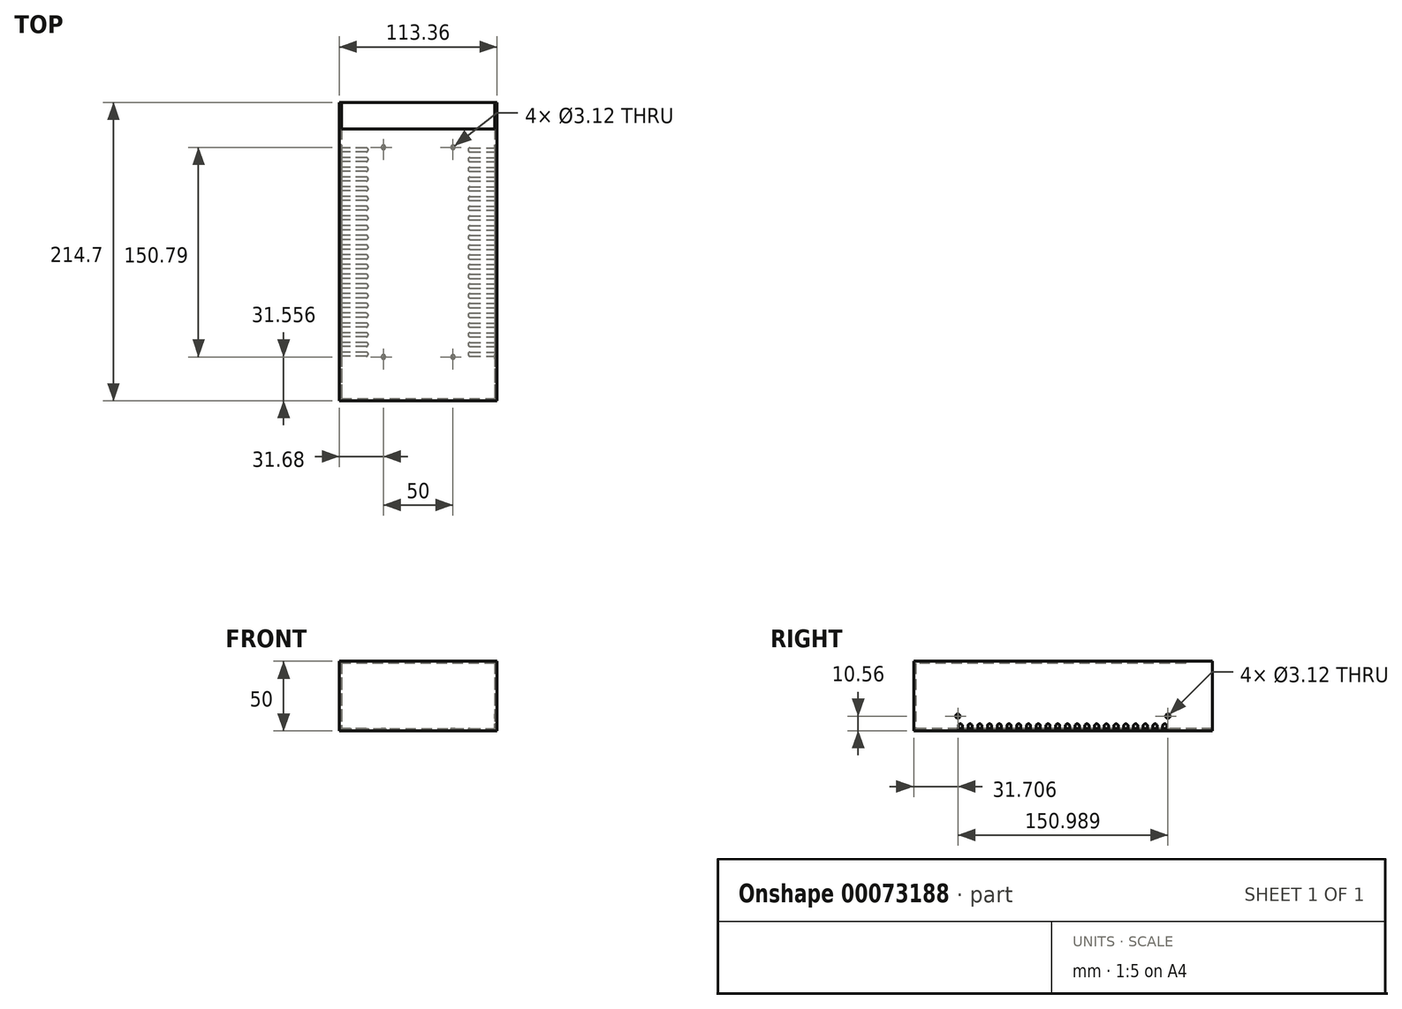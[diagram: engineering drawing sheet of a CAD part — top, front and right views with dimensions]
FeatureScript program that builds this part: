
annotation { "Feature Type Name" : "Feature", "Feature Type Description" : "" }
export const myFeature = defineFeature(function(context is Context, id is Id, definition is map)
    precondition{}
    {
        {
            var Q0;
            Q0=qCreatedBy(makeId("Top.planeOp"),FACE);
            var sketch = newSketch(context, id + "F0", { "sketchPlane" : qUnion([Q0])});
            skLineSegment(sketch, "E0.bottom", {"start": v(-56.68, 107.35) * mm, "end": v(56.67, 107.35) * mm});
            skLineSegment(sketch, "E0.top", {"start": v(-56.67, -107.35) * mm, "end": v(56.68, -107.35) * mm});
            skLineSegment(sketch, "E0.left", {"start": v(-56.68, 107.35) * mm, "end": v(-56.67, -107.35) * mm});
            skLineSegment(sketch, "E0.right", {"start": v(56.67, 107.35) * mm, "end": v(56.68, -107.35) * mm});
            skSolve(sketch);
        }
        {
            var Q0;
            Q0 = qSketchRegion(id + "F0", true);
            extrude(context, id + "F1", {"entities" : qUnion([Q0]), "depth" : 50 * mm});
        }
        {
            var Q0;
            Q0=makeQuery(id+"F1.opExtrude","CAP_FACE",FACE,{"disambiguationData":[OSD([sQuery(id+"F0.wireOp",EDGE,"E0.bottom"),sQuery(id+"F0.wireOp",EDGE,"E0.top"),sQuery(id+"F0.wireOp",EDGE,"E0.left"),sQuery(id+"F0.wireOp",EDGE,"E0.right")])],"isStart":true});
            var sketch = newSketch(context, id + "F2", { "sketchPlane" : qUnion([Q0])});
            skCircle(sketch, "E1", {"center": v(25, -75) * mm, "radius": 1.56 * mm});
            skCircle(sketch, "E2", {"center": v(-25, -75) * mm, "radius": 1.56 * mm});
            skCircle(sketch, "E3", {"center": v(25, 75.8) * mm, "radius": 1.56 * mm});
            skCircle(sketch, "E4", {"center": v(-25, 75.8) * mm, "radius": 1.56 * mm});
            skSolve(sketch);
        }
        {
            var Q0;
            Q0=makeQuery(id+"F1.opExtrude","SWEPT_FACE",FACE,{"disambiguationData":[OSD([sQuery(id+"F0.wireOp",EDGE,"E0.bottom")])]});
            shell(context, id + "F3", {"entities" : qUnion([Q0]), "thickness" : 1.5 * mm});
        }
        {
            var Q0;
            Q0 = qSketchRegion(id + "F2", true);
            extrude(context, id + "F4", {"entities" : qUnion([Q0]), "operationType" : NewBodyOperationType.REMOVE, "endBound" : BoundingType.UP_TO_NEXT, "oppositeDirection" : true, "depth" : 25 * mm});
        }
        {
            var Q0;
            Q0=makeQuery(id+"F1.opExtrude","CAP_FACE",FACE,{"disambiguationData":[OSD([sQuery(id+"F0.wireOp",EDGE,"E0.bottom"),sQuery(id+"F0.wireOp",EDGE,"E0.top"),sQuery(id+"F0.wireOp",EDGE,"E0.left"),sQuery(id+"F0.wireOp",EDGE,"E0.right")])],"isStart":true});
            var sketch = newSketch(context, id + "F5", { "sketchPlane" : qUnion([Q0])});
            skLineSegment(sketch, "E5.bottom", {"start": v(-37.4, 72.35) * mm, "end": v(-56.67, 72.35) * mm});
            skLineSegment(sketch, "E5.top", {"start": v(-37.4, 75.35) * mm, "end": v(-56.67, 75.35) * mm});
            skLineSegment(sketch, "E5.left", {"start": v(-37.4, 72.35) * mm, "end": v(-37.4, 75.35) * mm});
            skLineSegment(sketch, "E5.right", {"start": v(-56.67, 72.35) * mm, "end": v(-56.67, 75.35) * mm});
            skCircle(sketch, "E6", {"center": v(-37.4, 73.85) * mm, "radius": 1.5 * mm});
            skLineSegment(sketch, "E7.MirrorCS", {"start": v(37.4, 72.35) * mm, "end": v(56.67, 72.35) * mm});
            skLineSegment(sketch, "E8.MirrorCS", {"start": v(37.4, 75.35) * mm, "end": v(56.67, 75.35) * mm});
            skLineSegment(sketch, "E9.MirrorCS", {"start": v(56.67, 72.35) * mm, "end": v(56.67, 75.35) * mm});
            skCircle(sketch, "E10.MirrorC", {"center": v(37.4, 73.85) * mm, "radius": 1.5 * mm});
            skLineSegment(sketch, "E11.0.1.0", {"start": v(-37.4, 65.35) * mm, "end": v(-56.67, 65.35) * mm});
            skCircle(sketch, "E11.0.1.1", {"center": v(-37.4, 66.85) * mm, "radius": 1.5 * mm});
            skLineSegment(sketch, "E11.0.1.2", {"start": v(-37.4, 68.35) * mm, "end": v(-56.67, 68.35) * mm});
            skLineSegment(sketch, "E11.0.1.3", {"start": v(-56.67, 65.35) * mm, "end": v(-56.67, 68.35) * mm});
            skCircle(sketch, "E11.0.1.4", {"center": v(37.4, 66.85) * mm, "radius": 1.5 * mm});
            skLineSegment(sketch, "E11.0.1.5", {"start": v(37.4, 65.35) * mm, "end": v(56.67, 65.35) * mm});
            skLineSegment(sketch, "E11.0.1.6", {"start": v(37.4, 68.35) * mm, "end": v(56.67, 68.35) * mm});
            skLineSegment(sketch, "E11.0.1.7", {"start": v(56.67, 65.35) * mm, "end": v(56.67, 68.35) * mm});
            skLineSegment(sketch, "E11.0.2.0", {"start": v(-37.4, 58.35) * mm, "end": v(-56.67, 58.35) * mm});
            skCircle(sketch, "E11.0.2.1", {"center": v(-37.4, 59.85) * mm, "radius": 1.5 * mm});
            skLineSegment(sketch, "E11.0.2.2", {"start": v(-37.4, 61.35) * mm, "end": v(-56.67, 61.35) * mm});
            skLineSegment(sketch, "E11.0.2.3", {"start": v(-56.67, 58.35) * mm, "end": v(-56.67, 61.35) * mm});
            skCircle(sketch, "E11.0.2.4", {"center": v(37.4, 59.85) * mm, "radius": 1.5 * mm});
            skLineSegment(sketch, "E11.0.2.5", {"start": v(37.4, 58.35) * mm, "end": v(56.67, 58.35) * mm});
            skLineSegment(sketch, "E11.0.2.6", {"start": v(37.4, 61.35) * mm, "end": v(56.67, 61.35) * mm});
            skLineSegment(sketch, "E11.0.2.7", {"start": v(56.67, 58.35) * mm, "end": v(56.67, 61.35) * mm});
            skLineSegment(sketch, "E11.0.3.0", {"start": v(-37.4, 51.35) * mm, "end": v(-56.67, 51.35) * mm});
            skCircle(sketch, "E11.0.3.1", {"center": v(-37.4, 52.85) * mm, "radius": 1.5 * mm});
            skLineSegment(sketch, "E11.0.3.2", {"start": v(-37.4, 54.35) * mm, "end": v(-56.67, 54.35) * mm});
            skLineSegment(sketch, "E11.0.3.3", {"start": v(-56.67, 51.35) * mm, "end": v(-56.67, 54.35) * mm});
            skCircle(sketch, "E11.0.3.4", {"center": v(37.4, 52.85) * mm, "radius": 1.5 * mm});
            skLineSegment(sketch, "E11.0.3.5", {"start": v(37.4, 51.35) * mm, "end": v(56.67, 51.35) * mm});
            skLineSegment(sketch, "E11.0.3.6", {"start": v(37.4, 54.35) * mm, "end": v(56.67, 54.35) * mm});
            skLineSegment(sketch, "E11.0.3.7", {"start": v(56.67, 51.35) * mm, "end": v(56.67, 54.35) * mm});
            skLineSegment(sketch, "E11.0.4.0", {"start": v(-37.4, 44.35) * mm, "end": v(-56.67, 44.35) * mm});
            skCircle(sketch, "E11.0.4.1", {"center": v(-37.4, 45.85) * mm, "radius": 1.5 * mm});
            skLineSegment(sketch, "E11.0.4.2", {"start": v(-37.4, 47.35) * mm, "end": v(-56.67, 47.35) * mm});
            skLineSegment(sketch, "E11.0.4.3", {"start": v(-56.67, 44.35) * mm, "end": v(-56.67, 47.35) * mm});
            skCircle(sketch, "E11.0.4.4", {"center": v(37.4, 45.85) * mm, "radius": 1.5 * mm});
            skLineSegment(sketch, "E11.0.4.5", {"start": v(37.4, 44.35) * mm, "end": v(56.67, 44.35) * mm});
            skLineSegment(sketch, "E11.0.4.6", {"start": v(37.4, 47.35) * mm, "end": v(56.67, 47.35) * mm});
            skLineSegment(sketch, "E11.0.4.7", {"start": v(56.67, 44.35) * mm, "end": v(56.67, 47.35) * mm});
            skLineSegment(sketch, "E11.0.5.0", {"start": v(-37.4, 37.35) * mm, "end": v(-56.67, 37.35) * mm});
            skCircle(sketch, "E11.0.5.1", {"center": v(-37.4, 38.85) * mm, "radius": 1.5 * mm});
            skLineSegment(sketch, "E11.0.5.2", {"start": v(-37.4, 40.35) * mm, "end": v(-56.67, 40.35) * mm});
            skLineSegment(sketch, "E11.0.5.3", {"start": v(-56.67, 37.35) * mm, "end": v(-56.67, 40.35) * mm});
            skCircle(sketch, "E11.0.5.4", {"center": v(37.4, 38.85) * mm, "radius": 1.5 * mm});
            skLineSegment(sketch, "E11.0.5.5", {"start": v(37.4, 37.35) * mm, "end": v(56.67, 37.35) * mm});
            skLineSegment(sketch, "E11.0.5.6", {"start": v(37.4, 40.35) * mm, "end": v(56.67, 40.35) * mm});
            skLineSegment(sketch, "E11.0.5.7", {"start": v(56.67, 37.35) * mm, "end": v(56.67, 40.35) * mm});
            skLineSegment(sketch, "E11.0.6.0", {"start": v(-37.4, 30.35) * mm, "end": v(-56.67, 30.35) * mm});
            skCircle(sketch, "E11.0.6.1", {"center": v(-37.4, 31.85) * mm, "radius": 1.5 * mm});
            skLineSegment(sketch, "E11.0.6.2", {"start": v(-37.4, 33.35) * mm, "end": v(-56.67, 33.35) * mm});
            skLineSegment(sketch, "E11.0.6.3", {"start": v(-56.67, 30.35) * mm, "end": v(-56.67, 33.35) * mm});
            skCircle(sketch, "E11.0.6.4", {"center": v(37.4, 31.85) * mm, "radius": 1.5 * mm});
            skLineSegment(sketch, "E11.0.6.5", {"start": v(37.4, 30.35) * mm, "end": v(56.67, 30.35) * mm});
            skLineSegment(sketch, "E11.0.6.6", {"start": v(37.4, 33.35) * mm, "end": v(56.67, 33.35) * mm});
            skLineSegment(sketch, "E11.0.6.7", {"start": v(56.67, 30.35) * mm, "end": v(56.67, 33.35) * mm});
            skLineSegment(sketch, "E11.0.7.0", {"start": v(-37.4, 23.35) * mm, "end": v(-56.67, 23.35) * mm});
            skCircle(sketch, "E11.0.7.1", {"center": v(-37.4, 24.85) * mm, "radius": 1.5 * mm});
            skLineSegment(sketch, "E11.0.7.2", {"start": v(-37.4, 26.35) * mm, "end": v(-56.67, 26.35) * mm});
            skLineSegment(sketch, "E11.0.7.3", {"start": v(-56.67, 23.35) * mm, "end": v(-56.67, 26.35) * mm});
            skCircle(sketch, "E11.0.7.4", {"center": v(37.4, 24.85) * mm, "radius": 1.5 * mm});
            skLineSegment(sketch, "E11.0.7.5", {"start": v(37.4, 23.35) * mm, "end": v(56.67, 23.35) * mm});
            skLineSegment(sketch, "E11.0.7.6", {"start": v(37.4, 26.35) * mm, "end": v(56.67, 26.35) * mm});
            skLineSegment(sketch, "E11.0.7.7", {"start": v(56.67, 23.35) * mm, "end": v(56.67, 26.35) * mm});
            skLineSegment(sketch, "E11.0.8.0", {"start": v(-37.4, 16.35) * mm, "end": v(-56.67, 16.35) * mm});
            skCircle(sketch, "E11.0.8.1", {"center": v(-37.4, 17.85) * mm, "radius": 1.5 * mm});
            skLineSegment(sketch, "E11.0.8.2", {"start": v(-37.4, 19.35) * mm, "end": v(-56.67, 19.35) * mm});
            skLineSegment(sketch, "E11.0.8.3", {"start": v(-56.67, 16.35) * mm, "end": v(-56.67, 19.35) * mm});
            skCircle(sketch, "E11.0.8.4", {"center": v(37.4, 17.85) * mm, "radius": 1.5 * mm});
            skLineSegment(sketch, "E11.0.8.5", {"start": v(37.4, 16.35) * mm, "end": v(56.67, 16.35) * mm});
            skLineSegment(sketch, "E11.0.8.6", {"start": v(37.4, 19.35) * mm, "end": v(56.67, 19.35) * mm});
            skLineSegment(sketch, "E11.0.8.7", {"start": v(56.67, 16.35) * mm, "end": v(56.67, 19.35) * mm});
            skLineSegment(sketch, "E11.0.9.0", {"start": v(-37.4, 9.35) * mm, "end": v(-56.67, 9.35) * mm});
            skCircle(sketch, "E11.0.9.1", {"center": v(-37.4, 10.85) * mm, "radius": 1.5 * mm});
            skLineSegment(sketch, "E11.0.9.2", {"start": v(-37.4, 12.35) * mm, "end": v(-56.67, 12.35) * mm});
            skLineSegment(sketch, "E11.0.9.3", {"start": v(-56.67, 9.35) * mm, "end": v(-56.67, 12.35) * mm});
            skCircle(sketch, "E11.0.9.4", {"center": v(37.4, 10.85) * mm, "radius": 1.5 * mm});
            skLineSegment(sketch, "E11.0.9.5", {"start": v(37.4, 9.35) * mm, "end": v(56.67, 9.35) * mm});
            skLineSegment(sketch, "E11.0.9.6", {"start": v(37.4, 12.35) * mm, "end": v(56.67, 12.35) * mm});
            skLineSegment(sketch, "E11.0.9.7", {"start": v(56.67, 9.35) * mm, "end": v(56.67, 12.35) * mm});
            skLineSegment(sketch, "E11.0.10.0", {"start": v(-37.4, 2.35) * mm, "end": v(-56.67, 2.35) * mm});
            skCircle(sketch, "E11.0.10.1", {"center": v(-37.4, 3.85) * mm, "radius": 1.5 * mm});
            skLineSegment(sketch, "E11.0.10.2", {"start": v(-37.4, 5.35) * mm, "end": v(-56.67, 5.35) * mm});
            skLineSegment(sketch, "E11.0.10.3", {"start": v(-56.67, 2.35) * mm, "end": v(-56.67, 5.35) * mm});
            skCircle(sketch, "E11.0.10.4", {"center": v(37.4, 3.85) * mm, "radius": 1.5 * mm});
            skLineSegment(sketch, "E11.0.10.5", {"start": v(37.4, 2.35) * mm, "end": v(56.67, 2.35) * mm});
            skLineSegment(sketch, "E11.0.10.6", {"start": v(37.4, 5.35) * mm, "end": v(56.67, 5.35) * mm});
            skLineSegment(sketch, "E11.0.10.7", {"start": v(56.67, 2.35) * mm, "end": v(56.67, 5.35) * mm});
            skLineSegment(sketch, "E11.0.11.0", {"start": v(-37.4, -4.65) * mm, "end": v(-56.67, -4.65) * mm});
            skCircle(sketch, "E11.0.11.1", {"center": v(-37.4, -3.15) * mm, "radius": 1.5 * mm});
            skLineSegment(sketch, "E11.0.11.2", {"start": v(-37.4, -1.65) * mm, "end": v(-56.67, -1.65) * mm});
            skLineSegment(sketch, "E11.0.11.3", {"start": v(-56.67, -4.65) * mm, "end": v(-56.67, -1.65) * mm});
            skCircle(sketch, "E11.0.11.4", {"center": v(37.4, -3.15) * mm, "radius": 1.5 * mm});
            skLineSegment(sketch, "E11.0.11.5", {"start": v(37.4, -4.65) * mm, "end": v(56.67, -4.65) * mm});
            skLineSegment(sketch, "E11.0.11.6", {"start": v(37.4, -1.65) * mm, "end": v(56.67, -1.65) * mm});
            skLineSegment(sketch, "E11.0.11.7", {"start": v(56.67, -4.65) * mm, "end": v(56.67, -1.65) * mm});
            skLineSegment(sketch, "E11.0.12.0", {"start": v(-37.4, -11.65) * mm, "end": v(-56.67, -11.65) * mm});
            skCircle(sketch, "E11.0.12.1", {"center": v(-37.4, -10.15) * mm, "radius": 1.5 * mm});
            skLineSegment(sketch, "E11.0.12.2", {"start": v(-37.4, -8.65) * mm, "end": v(-56.67, -8.65) * mm});
            skLineSegment(sketch, "E11.0.12.3", {"start": v(-56.67, -11.65) * mm, "end": v(-56.67, -8.65) * mm});
            skCircle(sketch, "E11.0.12.4", {"center": v(37.4, -10.15) * mm, "radius": 1.5 * mm});
            skLineSegment(sketch, "E11.0.12.5", {"start": v(37.4, -11.65) * mm, "end": v(56.67, -11.65) * mm});
            skLineSegment(sketch, "E11.0.12.6", {"start": v(37.4, -8.65) * mm, "end": v(56.67, -8.65) * mm});
            skLineSegment(sketch, "E11.0.12.7", {"start": v(56.67, -11.65) * mm, "end": v(56.67, -8.65) * mm});
            skLineSegment(sketch, "E11.0.13.0", {"start": v(-37.4, -18.65) * mm, "end": v(-56.67, -18.65) * mm});
            skCircle(sketch, "E11.0.13.1", {"center": v(-37.4, -17.15) * mm, "radius": 1.5 * mm});
            skLineSegment(sketch, "E11.0.13.2", {"start": v(-37.4, -15.65) * mm, "end": v(-56.67, -15.65) * mm});
            skLineSegment(sketch, "E11.0.13.3", {"start": v(-56.67, -18.65) * mm, "end": v(-56.67, -15.65) * mm});
            skCircle(sketch, "E11.0.13.4", {"center": v(37.4, -17.15) * mm, "radius": 1.5 * mm});
            skLineSegment(sketch, "E11.0.13.5", {"start": v(37.4, -18.65) * mm, "end": v(56.67, -18.65) * mm});
            skLineSegment(sketch, "E11.0.13.6", {"start": v(37.4, -15.65) * mm, "end": v(56.67, -15.65) * mm});
            skLineSegment(sketch, "E11.0.13.7", {"start": v(56.67, -18.65) * mm, "end": v(56.67, -15.65) * mm});
            skLineSegment(sketch, "E11.0.14.0", {"start": v(-37.4, -25.65) * mm, "end": v(-56.67, -25.65) * mm});
            skCircle(sketch, "E11.0.14.1", {"center": v(-37.4, -24.15) * mm, "radius": 1.5 * mm});
            skLineSegment(sketch, "E11.0.14.2", {"start": v(-37.4, -22.65) * mm, "end": v(-56.67, -22.65) * mm});
            skLineSegment(sketch, "E11.0.14.3", {"start": v(-56.67, -25.65) * mm, "end": v(-56.67, -22.65) * mm});
            skCircle(sketch, "E11.0.14.4", {"center": v(37.4, -24.15) * mm, "radius": 1.5 * mm});
            skLineSegment(sketch, "E11.0.14.5", {"start": v(37.4, -25.65) * mm, "end": v(56.67, -25.65) * mm});
            skLineSegment(sketch, "E11.0.14.6", {"start": v(37.4, -22.65) * mm, "end": v(56.67, -22.65) * mm});
            skLineSegment(sketch, "E11.0.14.7", {"start": v(56.67, -25.65) * mm, "end": v(56.67, -22.65) * mm});
            skLineSegment(sketch, "E11.0.15.0", {"start": v(-37.4, -32.65) * mm, "end": v(-56.67, -32.65) * mm});
            skCircle(sketch, "E11.0.15.1", {"center": v(-37.4, -31.15) * mm, "radius": 1.5 * mm});
            skLineSegment(sketch, "E11.0.15.2", {"start": v(-37.4, -29.65) * mm, "end": v(-56.67, -29.65) * mm});
            skLineSegment(sketch, "E11.0.15.3", {"start": v(-56.67, -32.65) * mm, "end": v(-56.67, -29.65) * mm});
            skCircle(sketch, "E11.0.15.4", {"center": v(37.4, -31.15) * mm, "radius": 1.5 * mm});
            skLineSegment(sketch, "E11.0.15.5", {"start": v(37.4, -32.65) * mm, "end": v(56.67, -32.65) * mm});
            skLineSegment(sketch, "E11.0.15.6", {"start": v(37.4, -29.65) * mm, "end": v(56.67, -29.65) * mm});
            skLineSegment(sketch, "E11.0.15.7", {"start": v(56.67, -32.65) * mm, "end": v(56.67, -29.65) * mm});
            skLineSegment(sketch, "E11.0.16.0", {"start": v(-37.4, -39.65) * mm, "end": v(-56.67, -39.65) * mm});
            skCircle(sketch, "E11.0.16.1", {"center": v(-37.4, -38.15) * mm, "radius": 1.5 * mm});
            skLineSegment(sketch, "E11.0.16.2", {"start": v(-37.4, -36.65) * mm, "end": v(-56.67, -36.65) * mm});
            skLineSegment(sketch, "E11.0.16.3", {"start": v(-56.67, -39.65) * mm, "end": v(-56.67, -36.65) * mm});
            skCircle(sketch, "E11.0.16.4", {"center": v(37.4, -38.15) * mm, "radius": 1.5 * mm});
            skLineSegment(sketch, "E11.0.16.5", {"start": v(37.4, -39.65) * mm, "end": v(56.67, -39.65) * mm});
            skLineSegment(sketch, "E11.0.16.6", {"start": v(37.4, -36.65) * mm, "end": v(56.67, -36.65) * mm});
            skLineSegment(sketch, "E11.0.16.7", {"start": v(56.67, -39.65) * mm, "end": v(56.67, -36.65) * mm});
            skLineSegment(sketch, "E11.0.17.0", {"start": v(-37.4, -46.65) * mm, "end": v(-56.67, -46.65) * mm});
            skCircle(sketch, "E11.0.17.1", {"center": v(-37.4, -45.15) * mm, "radius": 1.5 * mm});
            skLineSegment(sketch, "E11.0.17.2", {"start": v(-37.4, -43.65) * mm, "end": v(-56.67, -43.65) * mm});
            skLineSegment(sketch, "E11.0.17.3", {"start": v(-56.67, -46.65) * mm, "end": v(-56.67, -43.65) * mm});
            skCircle(sketch, "E11.0.17.4", {"center": v(37.4, -45.15) * mm, "radius": 1.5 * mm});
            skLineSegment(sketch, "E11.0.17.5", {"start": v(37.4, -46.65) * mm, "end": v(56.67, -46.65) * mm});
            skLineSegment(sketch, "E11.0.17.6", {"start": v(37.4, -43.65) * mm, "end": v(56.67, -43.65) * mm});
            skLineSegment(sketch, "E11.0.17.7", {"start": v(56.67, -46.65) * mm, "end": v(56.67, -43.65) * mm});
            skLineSegment(sketch, "E11.0.18.0", {"start": v(-37.4, -53.65) * mm, "end": v(-56.67, -53.65) * mm});
            skCircle(sketch, "E11.0.18.1", {"center": v(-37.4, -52.15) * mm, "radius": 1.5 * mm});
            skLineSegment(sketch, "E11.0.18.2", {"start": v(-37.4, -50.65) * mm, "end": v(-56.67, -50.65) * mm});
            skLineSegment(sketch, "E11.0.18.3", {"start": v(-56.67, -53.65) * mm, "end": v(-56.67, -50.65) * mm});
            skCircle(sketch, "E11.0.18.4", {"center": v(37.4, -52.15) * mm, "radius": 1.5 * mm});
            skLineSegment(sketch, "E11.0.18.5", {"start": v(37.4, -53.65) * mm, "end": v(56.67, -53.65) * mm});
            skLineSegment(sketch, "E11.0.18.6", {"start": v(37.4, -50.65) * mm, "end": v(56.67, -50.65) * mm});
            skLineSegment(sketch, "E11.0.18.7", {"start": v(56.67, -53.65) * mm, "end": v(56.67, -50.65) * mm});
            skLineSegment(sketch, "E11.0.19.0", {"start": v(-37.4, -60.65) * mm, "end": v(-56.67, -60.65) * mm});
            skCircle(sketch, "E11.0.19.1", {"center": v(-37.4, -59.15) * mm, "radius": 1.5 * mm});
            skLineSegment(sketch, "E11.0.19.2", {"start": v(-37.4, -57.65) * mm, "end": v(-56.67, -57.65) * mm});
            skLineSegment(sketch, "E11.0.19.3", {"start": v(-56.67, -60.65) * mm, "end": v(-56.67, -57.65) * mm});
            skCircle(sketch, "E11.0.19.4", {"center": v(37.4, -59.15) * mm, "radius": 1.5 * mm});
            skLineSegment(sketch, "E11.0.19.5", {"start": v(37.4, -60.65) * mm, "end": v(56.67, -60.65) * mm});
            skLineSegment(sketch, "E11.0.19.6", {"start": v(37.4, -57.65) * mm, "end": v(56.67, -57.65) * mm});
            skLineSegment(sketch, "E11.0.19.7", {"start": v(56.67, -60.65) * mm, "end": v(56.67, -57.65) * mm});
            skLineSegment(sketch, "E11.0.20.0", {"start": v(-37.4, -67.65) * mm, "end": v(-56.67, -67.65) * mm});
            skCircle(sketch, "E11.0.20.1", {"center": v(-37.4, -66.15) * mm, "radius": 1.5 * mm});
            skLineSegment(sketch, "E11.0.20.2", {"start": v(-37.4, -64.65) * mm, "end": v(-56.67, -64.65) * mm});
            skLineSegment(sketch, "E11.0.20.3", {"start": v(-56.67, -67.65) * mm, "end": v(-56.67, -64.65) * mm});
            skCircle(sketch, "E11.0.20.4", {"center": v(37.4, -66.15) * mm, "radius": 1.5 * mm});
            skLineSegment(sketch, "E11.0.20.5", {"start": v(37.4, -67.65) * mm, "end": v(56.67, -67.65) * mm});
            skLineSegment(sketch, "E11.0.20.6", {"start": v(37.4, -64.65) * mm, "end": v(56.67, -64.65) * mm});
            skLineSegment(sketch, "E11.0.20.7", {"start": v(56.67, -67.65) * mm, "end": v(56.67, -64.65) * mm});
            skLineSegment(sketch, "E11.0.21.0", {"start": v(-37.4, -74.65) * mm, "end": v(-56.67, -74.65) * mm});
            skCircle(sketch, "E11.0.21.1", {"center": v(-37.4, -73.15) * mm, "radius": 1.5 * mm});
            skLineSegment(sketch, "E11.0.21.2", {"start": v(-37.4, -71.65) * mm, "end": v(-56.67, -71.65) * mm});
            skLineSegment(sketch, "E11.0.21.3", {"start": v(-56.67, -74.65) * mm, "end": v(-56.67, -71.65) * mm});
            skCircle(sketch, "E11.0.21.4", {"center": v(37.4, -73.15) * mm, "radius": 1.5 * mm});
            skLineSegment(sketch, "E11.0.21.5", {"start": v(37.4, -74.65) * mm, "end": v(56.67, -74.65) * mm});
            skLineSegment(sketch, "E11.0.21.6", {"start": v(37.4, -71.65) * mm, "end": v(56.67, -71.65) * mm});
            skLineSegment(sketch, "E11.0.21.7", {"start": v(56.67, -74.65) * mm, "end": v(56.67, -71.65) * mm});
            skLineSegment(sketch, "E11.direction1", {"start": v(-56.67, 72.35) * mm, "end": v(-31.67, 72.35) * mm, "construction": true});
            skLineSegment(sketch, "E11.direction2", {"start": v(-56.67, 72.35) * mm, "end": v(-56.67, 65.35) * mm, "construction": true});
            skSolve(sketch);
        }
        {
            var Q0;
            Q0 = qSketchRegion(id + "F5", true);
            extrude(context, id + "F6", {"entities" : qUnion([Q0]), "operationType" : NewBodyOperationType.REMOVE, "oppositeDirection" : true, "depth" : 1.5 * mm});
        }
        {
            var Q0;
            Q0=makeQuery(id+"F1.opExtrude","CAP_FACE",FACE,{"disambiguationData":[OSD([sQuery(id+"F0.wireOp",EDGE,"E0.bottom"),sQuery(id+"F0.wireOp",EDGE,"E0.top"),sQuery(id+"F0.wireOp",EDGE,"E0.left"),sQuery(id+"F0.wireOp",EDGE,"E0.right")])],"isStart":false});
            var sketch = newSketch(context, id + "F7", { "sketchPlane" : qUnion([Q0])});
            skLineSegment(sketch, "E12.bottom", {"start": v(-55.18, 107.35) * mm, "end": v(55.18, 107.35) * mm});
            skLineSegment(sketch, "E12.top", {"start": v(-55.18, 88.23) * mm, "end": v(55.17, 88.23) * mm});
            skLineSegment(sketch, "E12.left", {"start": v(-55.18, 107.35) * mm, "end": v(-55.18, 88.23) * mm});
            skLineSegment(sketch, "E12.right", {"start": v(55.18, 107.35) * mm, "end": v(55.18, 88.23) * mm});
            skSolve(sketch);
        }
        {
            var Q0;
            Q0 = qSketchRegion(id + "F7", true);
            extrude(context, id + "F8", {"entities" : qUnion([Q0]), "operationType" : NewBodyOperationType.REMOVE, "endBound" : BoundingType.UP_TO_NEXT, "oppositeDirection" : true, "depth" : 25 * mm});
        }
        {
            var Q0;
            Q0=makeQuery(id+"F1.opExtrude","SWEPT_FACE",FACE,{"disambiguationData":[OSD([sQuery(id+"F0.wireOp",EDGE,"E0.right")])]});
            var sketch = newSketch(context, id + "F9", { "sketchPlane" : qUnion([Q0])});
            skLineSegment(sketch, "E13.bottom", {"start": v(71.65, 1.5) * mm, "end": v(74.65, 1.5) * mm});
            skLineSegment(sketch, "E13.left", {"start": v(71.65, 1.5) * mm, "end": v(71.65, 3.5) * mm});
            skLineSegment(sketch, "E13.right", {"start": v(74.65, 1.5) * mm, "end": v(74.65, 3.5) * mm});
            skArc(sketch, "E14", {"start": v(74.65, 3.5) * mm, "mid": v(73.15, 5) * mm, "end": v(71.65, 3.5) * mm});
            skLineSegment(sketch, "E15.1.0.0", {"start": v(64.65, 1.5) * mm, "end": v(64.65, 3.5) * mm});
            skLineSegment(sketch, "E15.1.0.1", {"start": v(67.65, 1.5) * mm, "end": v(67.65, 3.5) * mm});
            skLineSegment(sketch, "E15.1.0.2", {"start": v(64.65, 1.5) * mm, "end": v(67.65, 1.5) * mm});
            skArc(sketch, "E15.1.0.3", {"start": v(67.65, 3.5) * mm, "mid": v(66.15, 5) * mm, "end": v(64.65, 3.5) * mm});
            skLineSegment(sketch, "E15.2.0.0", {"start": v(57.65, 1.5) * mm, "end": v(57.65, 3.5) * mm});
            skLineSegment(sketch, "E15.2.0.1", {"start": v(60.65, 1.5) * mm, "end": v(60.65, 3.5) * mm});
            skLineSegment(sketch, "E15.2.0.2", {"start": v(57.65, 1.5) * mm, "end": v(60.65, 1.5) * mm});
            skArc(sketch, "E15.2.0.3", {"start": v(60.65, 3.5) * mm, "mid": v(59.15, 5) * mm, "end": v(57.65, 3.5) * mm});
            skLineSegment(sketch, "E15.3.0.0", {"start": v(50.65, 1.5) * mm, "end": v(50.65, 3.5) * mm});
            skLineSegment(sketch, "E15.3.0.1", {"start": v(53.65, 1.5) * mm, "end": v(53.65, 3.5) * mm});
            skLineSegment(sketch, "E15.3.0.2", {"start": v(50.65, 1.5) * mm, "end": v(53.65, 1.5) * mm});
            skArc(sketch, "E15.3.0.3", {"start": v(53.65, 3.5) * mm, "mid": v(52.15, 5) * mm, "end": v(50.65, 3.5) * mm});
            skLineSegment(sketch, "E15.4.0.0", {"start": v(43.65, 1.5) * mm, "end": v(43.65, 3.5) * mm});
            skLineSegment(sketch, "E15.4.0.1", {"start": v(46.65, 1.5) * mm, "end": v(46.65, 3.5) * mm});
            skLineSegment(sketch, "E15.4.0.2", {"start": v(43.65, 1.5) * mm, "end": v(46.65, 1.5) * mm});
            skArc(sketch, "E15.4.0.3", {"start": v(46.65, 3.5) * mm, "mid": v(45.15, 5) * mm, "end": v(43.65, 3.5) * mm});
            skLineSegment(sketch, "E15.5.0.0", {"start": v(36.65, 1.5) * mm, "end": v(36.65, 3.5) * mm});
            skLineSegment(sketch, "E15.5.0.1", {"start": v(39.65, 1.5) * mm, "end": v(39.65, 3.5) * mm});
            skLineSegment(sketch, "E15.5.0.2", {"start": v(36.65, 1.5) * mm, "end": v(39.65, 1.5) * mm});
            skArc(sketch, "E15.5.0.3", {"start": v(39.65, 3.5) * mm, "mid": v(38.15, 5) * mm, "end": v(36.65, 3.5) * mm});
            skLineSegment(sketch, "E15.6.0.0", {"start": v(29.65, 1.5) * mm, "end": v(29.65, 3.5) * mm});
            skLineSegment(sketch, "E15.6.0.1", {"start": v(32.65, 1.5) * mm, "end": v(32.65, 3.5) * mm});
            skLineSegment(sketch, "E15.6.0.2", {"start": v(29.65, 1.5) * mm, "end": v(32.65, 1.5) * mm});
            skArc(sketch, "E15.6.0.3", {"start": v(32.65, 3.5) * mm, "mid": v(31.15, 5) * mm, "end": v(29.65, 3.5) * mm});
            skLineSegment(sketch, "E15.7.0.0", {"start": v(22.65, 1.5) * mm, "end": v(22.65, 3.5) * mm});
            skLineSegment(sketch, "E15.7.0.1", {"start": v(25.65, 1.5) * mm, "end": v(25.65, 3.5) * mm});
            skLineSegment(sketch, "E15.7.0.2", {"start": v(22.65, 1.5) * mm, "end": v(25.65, 1.5) * mm});
            skArc(sketch, "E15.7.0.3", {"start": v(25.65, 3.5) * mm, "mid": v(24.15, 5) * mm, "end": v(22.65, 3.5) * mm});
            skLineSegment(sketch, "E15.8.0.0", {"start": v(15.65, 1.5) * mm, "end": v(15.65, 3.5) * mm});
            skLineSegment(sketch, "E15.8.0.1", {"start": v(18.65, 1.5) * mm, "end": v(18.65, 3.5) * mm});
            skLineSegment(sketch, "E15.8.0.2", {"start": v(15.65, 1.5) * mm, "end": v(18.65, 1.5) * mm});
            skArc(sketch, "E15.8.0.3", {"start": v(18.65, 3.5) * mm, "mid": v(17.15, 5) * mm, "end": v(15.65, 3.5) * mm});
            skLineSegment(sketch, "E15.9.0.0", {"start": v(8.65, 1.5) * mm, "end": v(8.65, 3.5) * mm});
            skLineSegment(sketch, "E15.9.0.1", {"start": v(11.65, 1.5) * mm, "end": v(11.65, 3.5) * mm});
            skLineSegment(sketch, "E15.9.0.2", {"start": v(8.65, 1.5) * mm, "end": v(11.65, 1.5) * mm});
            skArc(sketch, "E15.9.0.3", {"start": v(11.65, 3.5) * mm, "mid": v(10.15, 5) * mm, "end": v(8.65, 3.5) * mm});
            skLineSegment(sketch, "E15.10.0.0", {"start": v(1.65, 1.5) * mm, "end": v(1.65, 3.5) * mm});
            skLineSegment(sketch, "E15.10.0.1", {"start": v(4.65, 1.5) * mm, "end": v(4.65, 3.5) * mm});
            skLineSegment(sketch, "E15.10.0.2", {"start": v(1.65, 1.5) * mm, "end": v(4.65, 1.5) * mm});
            skArc(sketch, "E15.10.0.3", {"start": v(4.65, 3.5) * mm, "mid": v(3.15, 5) * mm, "end": v(1.65, 3.5) * mm});
            skLineSegment(sketch, "E15.11.0.0", {"start": v(-5.35, 1.5) * mm, "end": v(-5.35, 3.5) * mm});
            skLineSegment(sketch, "E15.11.0.1", {"start": v(-2.35, 1.5) * mm, "end": v(-2.35, 3.5) * mm});
            skLineSegment(sketch, "E15.11.0.2", {"start": v(-5.35, 1.5) * mm, "end": v(-2.35, 1.5) * mm});
            skArc(sketch, "E15.11.0.3", {"start": v(-2.35, 3.5) * mm, "mid": v(-3.85, 5) * mm, "end": v(-5.35, 3.5) * mm});
            skLineSegment(sketch, "E15.12.0.0", {"start": v(-12.35, 1.5) * mm, "end": v(-12.35, 3.5) * mm});
            skLineSegment(sketch, "E15.12.0.1", {"start": v(-9.35, 1.5) * mm, "end": v(-9.35, 3.5) * mm});
            skLineSegment(sketch, "E15.12.0.2", {"start": v(-12.35, 1.5) * mm, "end": v(-9.35, 1.5) * mm});
            skArc(sketch, "E15.12.0.3", {"start": v(-9.35, 3.5) * mm, "mid": v(-10.85, 5) * mm, "end": v(-12.35, 3.5) * mm});
            skLineSegment(sketch, "E15.13.0.0", {"start": v(-19.35, 1.5) * mm, "end": v(-19.35, 3.5) * mm});
            skLineSegment(sketch, "E15.13.0.1", {"start": v(-16.35, 1.5) * mm, "end": v(-16.35, 3.5) * mm});
            skLineSegment(sketch, "E15.13.0.2", {"start": v(-19.35, 1.5) * mm, "end": v(-16.35, 1.5) * mm});
            skArc(sketch, "E15.13.0.3", {"start": v(-16.35, 3.5) * mm, "mid": v(-17.85, 5) * mm, "end": v(-19.35, 3.5) * mm});
            skLineSegment(sketch, "E15.14.0.0", {"start": v(-26.35, 1.5) * mm, "end": v(-26.35, 3.5) * mm});
            skLineSegment(sketch, "E15.14.0.1", {"start": v(-23.35, 1.5) * mm, "end": v(-23.35, 3.5) * mm});
            skLineSegment(sketch, "E15.14.0.2", {"start": v(-26.35, 1.5) * mm, "end": v(-23.35, 1.5) * mm});
            skArc(sketch, "E15.14.0.3", {"start": v(-23.35, 3.5) * mm, "mid": v(-24.85, 5) * mm, "end": v(-26.35, 3.5) * mm});
            skLineSegment(sketch, "E15.15.0.0", {"start": v(-33.35, 1.5) * mm, "end": v(-33.35, 3.5) * mm});
            skLineSegment(sketch, "E15.15.0.1", {"start": v(-30.35, 1.5) * mm, "end": v(-30.35, 3.5) * mm});
            skLineSegment(sketch, "E15.15.0.2", {"start": v(-33.35, 1.5) * mm, "end": v(-30.35, 1.5) * mm});
            skArc(sketch, "E15.15.0.3", {"start": v(-30.35, 3.5) * mm, "mid": v(-31.85, 5) * mm, "end": v(-33.35, 3.5) * mm});
            skLineSegment(sketch, "E15.16.0.0", {"start": v(-40.35, 1.5) * mm, "end": v(-40.35, 3.5) * mm});
            skLineSegment(sketch, "E15.16.0.1", {"start": v(-37.35, 1.5) * mm, "end": v(-37.35, 3.5) * mm});
            skLineSegment(sketch, "E15.16.0.2", {"start": v(-40.35, 1.5) * mm, "end": v(-37.35, 1.5) * mm});
            skArc(sketch, "E15.16.0.3", {"start": v(-37.35, 3.5) * mm, "mid": v(-38.85, 5) * mm, "end": v(-40.35, 3.5) * mm});
            skLineSegment(sketch, "E15.17.0.0", {"start": v(-47.35, 1.5) * mm, "end": v(-47.35, 3.5) * mm});
            skLineSegment(sketch, "E15.17.0.1", {"start": v(-44.35, 1.5) * mm, "end": v(-44.35, 3.5) * mm});
            skLineSegment(sketch, "E15.17.0.2", {"start": v(-47.35, 1.5) * mm, "end": v(-44.35, 1.5) * mm});
            skArc(sketch, "E15.17.0.3", {"start": v(-44.35, 3.5) * mm, "mid": v(-45.85, 5) * mm, "end": v(-47.35, 3.5) * mm});
            skLineSegment(sketch, "E15.18.0.0", {"start": v(-54.35, 1.5) * mm, "end": v(-54.35, 3.5) * mm});
            skLineSegment(sketch, "E15.18.0.1", {"start": v(-51.35, 1.5) * mm, "end": v(-51.35, 3.5) * mm});
            skLineSegment(sketch, "E15.18.0.2", {"start": v(-54.35, 1.5) * mm, "end": v(-51.35, 1.5) * mm});
            skArc(sketch, "E15.18.0.3", {"start": v(-51.35, 3.5) * mm, "mid": v(-52.85, 5) * mm, "end": v(-54.35, 3.5) * mm});
            skLineSegment(sketch, "E15.19.0.0", {"start": v(-61.35, 1.5) * mm, "end": v(-61.35, 3.5) * mm});
            skLineSegment(sketch, "E15.19.0.1", {"start": v(-58.35, 1.5) * mm, "end": v(-58.35, 3.5) * mm});
            skLineSegment(sketch, "E15.19.0.2", {"start": v(-61.35, 1.5) * mm, "end": v(-58.35, 1.5) * mm});
            skArc(sketch, "E15.19.0.3", {"start": v(-58.35, 3.5) * mm, "mid": v(-59.85, 5) * mm, "end": v(-61.35, 3.5) * mm});
            skLineSegment(sketch, "E15.20.0.0", {"start": v(-68.35, 1.5) * mm, "end": v(-68.35, 3.5) * mm});
            skLineSegment(sketch, "E15.20.0.1", {"start": v(-65.35, 1.5) * mm, "end": v(-65.35, 3.5) * mm});
            skLineSegment(sketch, "E15.20.0.2", {"start": v(-68.35, 1.5) * mm, "end": v(-65.35, 1.5) * mm});
            skArc(sketch, "E15.20.0.3", {"start": v(-65.35, 3.5) * mm, "mid": v(-66.85, 5) * mm, "end": v(-68.35, 3.5) * mm});
            skLineSegment(sketch, "E15.21.0.0", {"start": v(-75.35, 1.5) * mm, "end": v(-75.35, 3.5) * mm});
            skLineSegment(sketch, "E15.21.0.1", {"start": v(-72.35, 1.5) * mm, "end": v(-72.35, 3.5) * mm});
            skLineSegment(sketch, "E15.21.0.2", {"start": v(-75.35, 1.5) * mm, "end": v(-72.35, 1.5) * mm});
            skArc(sketch, "E15.21.0.3", {"start": v(-72.35, 3.5) * mm, "mid": v(-73.85, 5) * mm, "end": v(-75.35, 3.5) * mm});
            skLineSegment(sketch, "E15.direction1", {"start": v(71.65, 1.5) * mm, "end": v(64.65, 1.5) * mm, "construction": true});
            skCircle(sketch, "E16", {"center": v(-75.64, 10.56) * mm, "radius": 1.56 * mm});
            skCircle(sketch, "E17", {"center": v(75.34, 10.56) * mm, "radius": 1.56 * mm});
            skSolve(sketch);
        }
        {
            var Q0;
            Q0 = qSketchRegion(id + "F9", true);
            extrude(context, id + "F10", {"entities" : qUnion([Q0]), "operationType" : NewBodyOperationType.REMOVE, "oppositeDirection" : true, "depth" : 1.5 * mm});
        }
        {
            var Q0;
            Q0=makeQuery(id+"F1.opExtrude","SWEPT_FACE",FACE,{"disambiguationData":[OSD([sQuery(id+"F0.wireOp",EDGE,"E0.left")])]});
            var sketch = newSketch(context, id + "F11", { "sketchPlane" : qUnion([Q0])});
            skCircle(sketch, "E18", {"center": v(-75.34, 10.56) * mm, "radius": 1.56 * mm});
            skCircle(sketch, "E19", {"center": v(75.64, 10.56) * mm, "radius": 1.56 * mm});
            skSolve(sketch);
        }
        {
            var Q0;
            Q0 = qSketchRegion(id + "F11", true);
            extrude(context, id + "F12", {"entities" : qUnion([Q0]), "operationType" : NewBodyOperationType.REMOVE, "oppositeDirection" : true, "depth" : 1.5 * mm});
        }
    });
